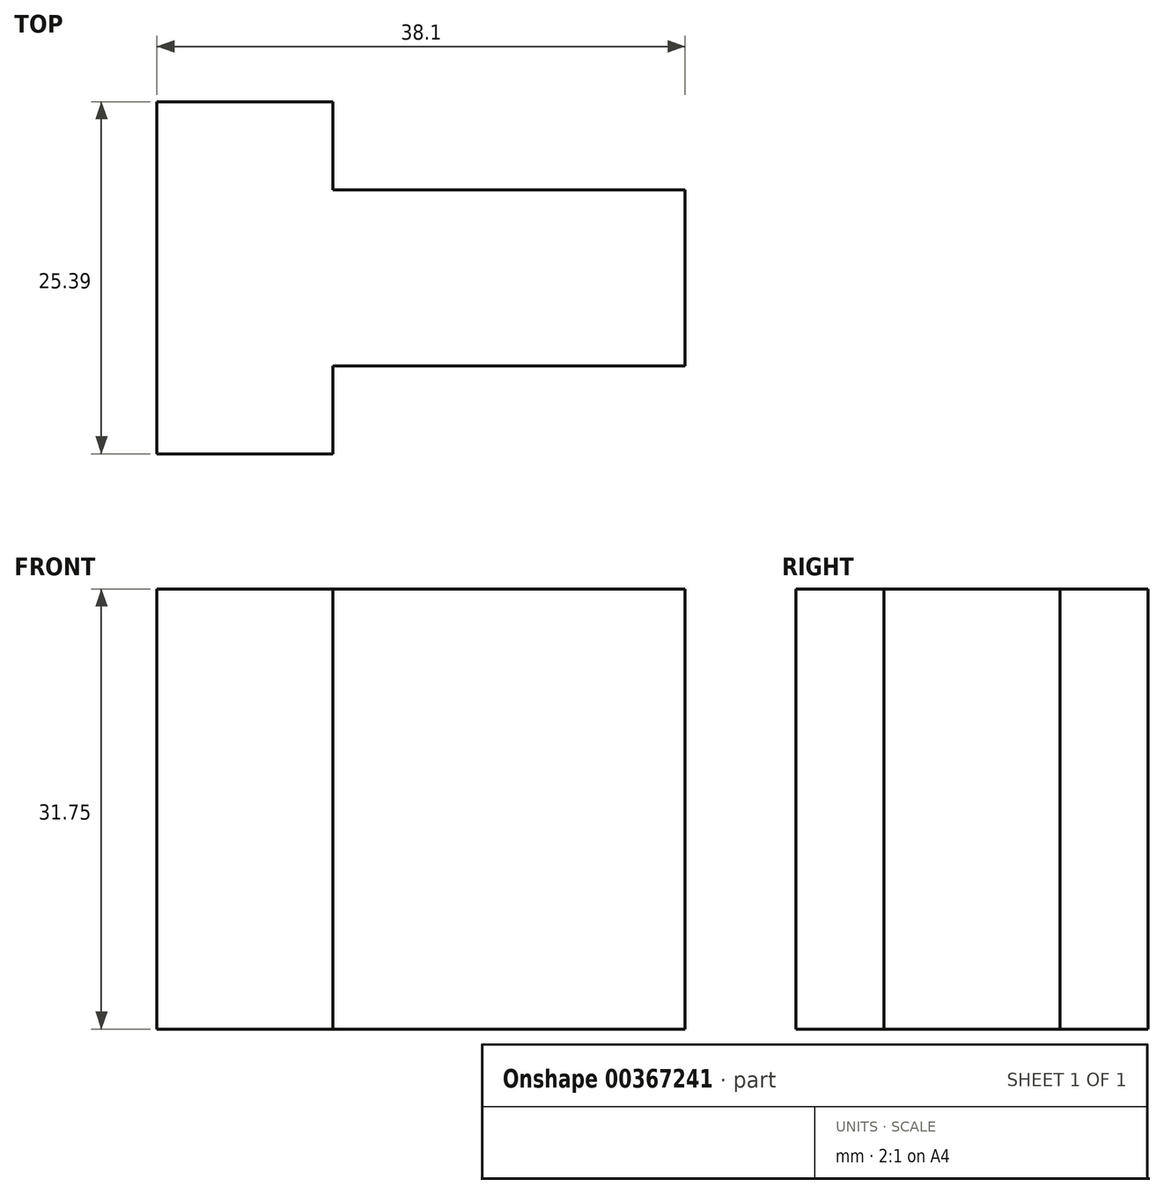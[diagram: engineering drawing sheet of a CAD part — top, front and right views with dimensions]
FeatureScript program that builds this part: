
annotation { "Feature Type Name" : "Feature", "Feature Type Description" : "" }
export const myFeature = defineFeature(function(context is Context, id is Id, definition is map)
    precondition{}
    {
        {
            var Q0;
            Q0=qCreatedBy(makeId("Top.planeOp"),FACE);
            var sketch = newSketch(context, id + "F0", { "sketchPlane" : qUnion([Q0])});
            skLineSegment(sketch, "E0", {"start": v(0, 0) * mm, "end": v(0, 25.4) * mm});
            skLineSegment(sketch, "E1", {"start": v(12.7, 25.4) * mm, "end": v(0, 25.4) * mm});
            skLineSegment(sketch, "E2", {"start": v(12.7, 25.4) * mm, "end": v(12.7, 19.04) * mm});
            skLineSegment(sketch, "E3", {"start": v(38.1, 19.04) * mm, "end": v(12.7, 19.04) * mm});
            skLineSegment(sketch, "E4", {"start": v(38.1, 19.04) * mm, "end": v(38.1, 6.34) * mm});
            skLineSegment(sketch, "E5", {"start": v(38.1, 6.34) * mm, "end": v(12.7, 6.34) * mm});
            skLineSegment(sketch, "E6", {"start": v(12.7, 6.34) * mm, "end": v(12.7, 0) * mm});
            skLineSegment(sketch, "E7", {"start": v(12.7, 0) * mm, "end": v(0, 0) * mm});
            skSolve(sketch);
        }
        {
            var Q0;
            Q0=makeQuery(id+"F0.imprint","IMPRINT",FACE,{"disambiguationData":[TD([[makeQuery(id+"F0.imprint","IMPRINT",EDGE,{"derivedFrom":sQuery(id+"F0.wireOp",EDGE,"E0")}),-1.0]])]});
            extrude(context, id + "F1", {"entities" : qUnion([Q0]), "oppositeDirection" : true, "depth" : 31.75 * mm});
        }
    });
